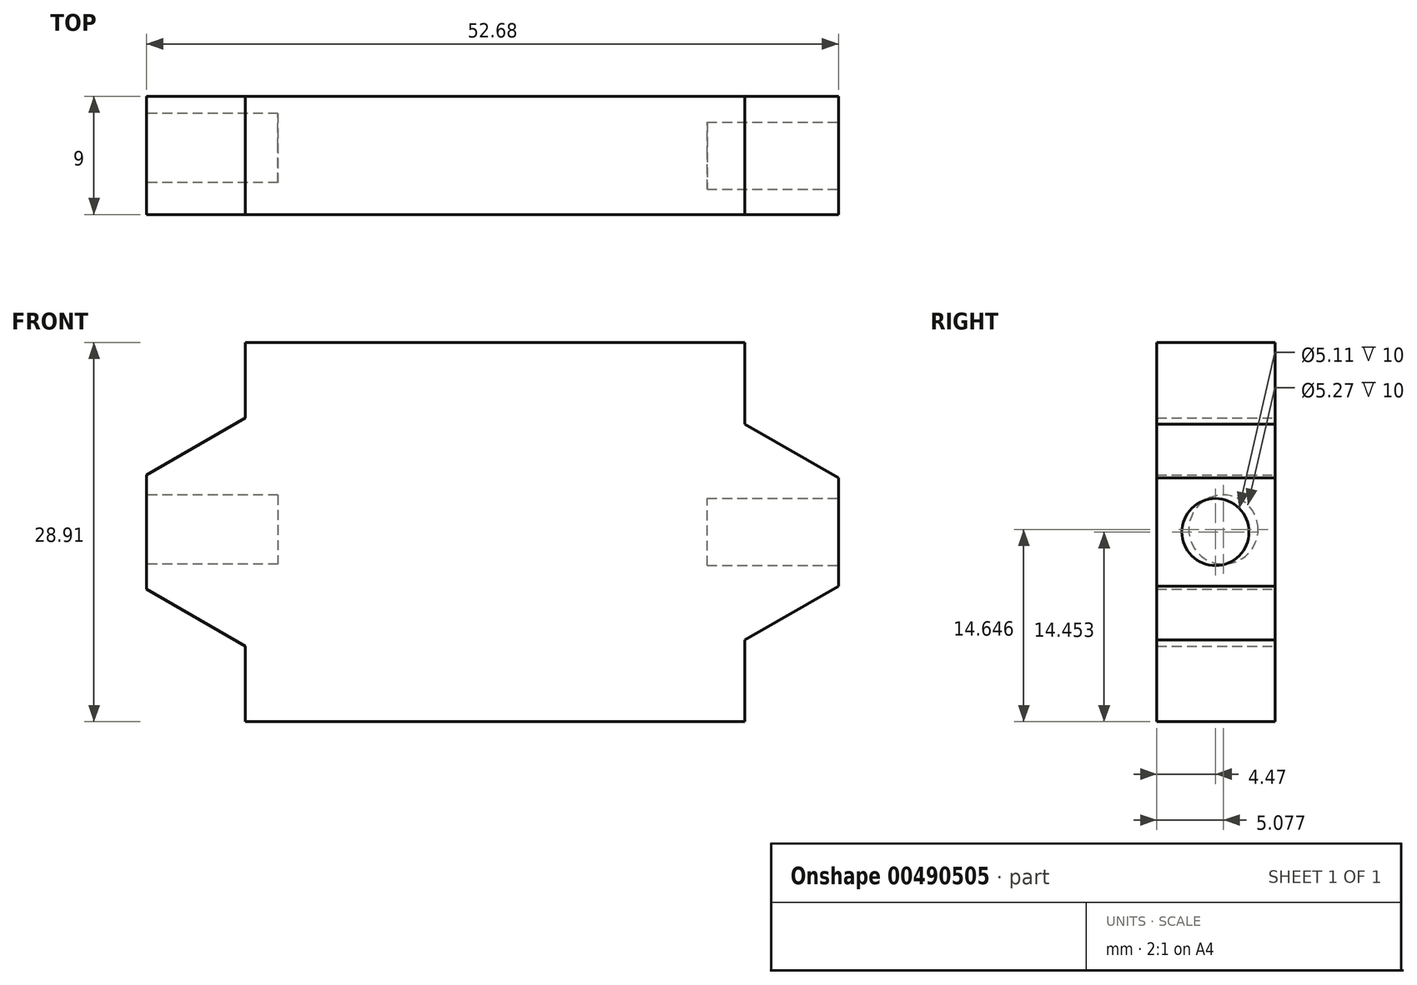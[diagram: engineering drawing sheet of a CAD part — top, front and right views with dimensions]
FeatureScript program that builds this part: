
annotation { "Feature Type Name" : "Feature", "Feature Type Description" : "" }
export const myFeature = defineFeature(function(context is Context, id is Id, definition is map)
    precondition{}
    {
        {
            var Q0;
            Q0=qCreatedBy(makeId("Front.planeOp"),FACE);
            var sketch = newSketch(context, id + "F0", { "sketchPlane" : qUnion([Q0])});
            skLineSegment(sketch, "E0.bottom", {"start": v(-53.27, 47.53) * mm, "end": v(-15.25, 47.53) * mm});
            skLineSegment(sketch, "E0.top", {"start": v(-53.27, 18.62) * mm, "end": v(-15.25, 18.62) * mm});
            skLineSegment(sketch, "E0.left", {"start": v(-53.27, 47.53) * mm, "end": v(-53.27, 18.62) * mm});
            skLineSegment(sketch, "E0.right", {"start": v(-15.25, 47.53) * mm, "end": v(-15.25, 18.62) * mm});
            skCircle(sketch, "E1.cCircle", {"center": v(-53.27, 33.07) * mm, "radius": 7.53 * mm, "construction": true});
            skLineSegment(sketch, "E1.0", {"start": v(-60.8, 28.73) * mm, "end": v(-60.8, 37.42) * mm});
            skLineSegment(sketch, "E1.1", {"start": v(-60.8, 37.42) * mm, "end": v(-53.27, 41.76) * mm});
            skLineSegment(sketch, "E1.2", {"start": v(-53.27, 41.76) * mm, "end": v(-45.75, 37.42) * mm});
            skLineSegment(sketch, "E1.3", {"start": v(-45.75, 37.42) * mm, "end": v(-45.75, 28.73) * mm});
            skLineSegment(sketch, "E1.4", {"start": v(-45.75, 28.73) * mm, "end": v(-53.27, 24.38) * mm});
            skLineSegment(sketch, "E1.5", {"start": v(-53.27, 24.38) * mm, "end": v(-60.8, 28.73) * mm});
            skPoint(sketch, "E1.0.midPoint", {"position": v(-60.8, 33.07) * mm});
            skCircle(sketch, "E2.cCircle", {"center": v(-15.25, 33.07) * mm, "radius": 7.13 * mm, "construction": true});
            skLineSegment(sketch, "E2.0", {"start": v(-22.38, 28.96) * mm, "end": v(-22.38, 37.19) * mm});
            skLineSegment(sketch, "E2.1", {"start": v(-22.38, 37.19) * mm, "end": v(-15.25, 41.3) * mm});
            skLineSegment(sketch, "E2.2", {"start": v(-15.25, 41.3) * mm, "end": v(-8.12, 37.19) * mm});
            skLineSegment(sketch, "E2.3", {"start": v(-8.12, 37.19) * mm, "end": v(-8.12, 28.96) * mm});
            skLineSegment(sketch, "E2.4", {"start": v(-8.12, 28.96) * mm, "end": v(-15.25, 24.84) * mm});
            skLineSegment(sketch, "E2.5", {"start": v(-15.25, 24.84) * mm, "end": v(-22.38, 28.96) * mm});
            skPoint(sketch, "E2.0.midPoint", {"position": v(-22.38, 33.07) * mm});
            skSolve(sketch);
        }
        {
            var Q0;
            {var subQ0=sQuery(id+"F0.wireOp",EDGE,"E1.3");Q0=makeQuery(id+"F0.imprint","IMPRINT",FACE,{"disambiguationData":[TD([[makeQuery(id+"F0.imprint","IMPRINT",EDGE,{"derivedFrom":subQ0}),1.0]])]});}
            var Q1;
            Q1 = qSketchRegion(id + "F0", true);
            extrude(context, id + "F1", {"entities" : qUnion([Q0, Q1]), "depth" : 9 * mm});
        }
        {
            var Q0;
            Q0=makeQuery(id+"F1.opExtrude","SWEPT_FACE",FACE,{"disambiguationData":[OSD([sQuery(id+"F0.wireOp",EDGE,"E2.3")])]});
            var sketch = newSketch(context, id + "F2", { "sketchPlane" : qUnion([Q0])});
            skCircle(sketch, "E3", {"center": v(-4.53, 33.07) * mm, "radius": 2.56 * mm});
            skPoint(sketch, "E3.centerSnap0", {"position": v(-9, 33.07) * mm});
            skSolve(sketch);
        }
        {
            var Q0;
            Q0=makeQuery(id+"F1.opExtrude","SWEPT_FACE",FACE,{"disambiguationData":[OSD([sQuery(id+"F0.wireOp",EDGE,"E1.0")])]});
            var sketch = newSketch(context, id + "F3", { "sketchPlane" : qUnion([Q0])});
            skCircle(sketch, "E4", {"center": v(3.92, 33.27) * mm, "radius": 2.63 * mm});
            skSolve(sketch);
        }
        {
            var Q0;
            Q0=makeQuery(id+"F2.imprint","IMPRINT",FACE,{"disambiguationData":[TD([[makeQuery(id+"F2.imprint","IMPRINT",EDGE,{"derivedFrom":sQuery(id+"F2.wireOp",EDGE,"E3")}),1.0]])]});
            extrude(context, id + "F4", {"entities" : qUnion([Q0]), "operationType" : NewBodyOperationType.REMOVE, "oppositeDirection" : true, "depth" : 10 * mm});
        }
        {
            var Q0;
            Q0=makeQuery(id+"F3.imprint","IMPRINT",FACE,{"disambiguationData":[TD([[makeQuery(id+"F3.imprint","IMPRINT",EDGE,{"derivedFrom":sQuery(id+"F3.wireOp",EDGE,"E4")}),1.0]])]});
            extrude(context, id + "F5", {"entities" : qUnion([Q0]), "operationType" : NewBodyOperationType.REMOVE, "oppositeDirection" : true, "depth" : 10 * mm});
        }
    });
